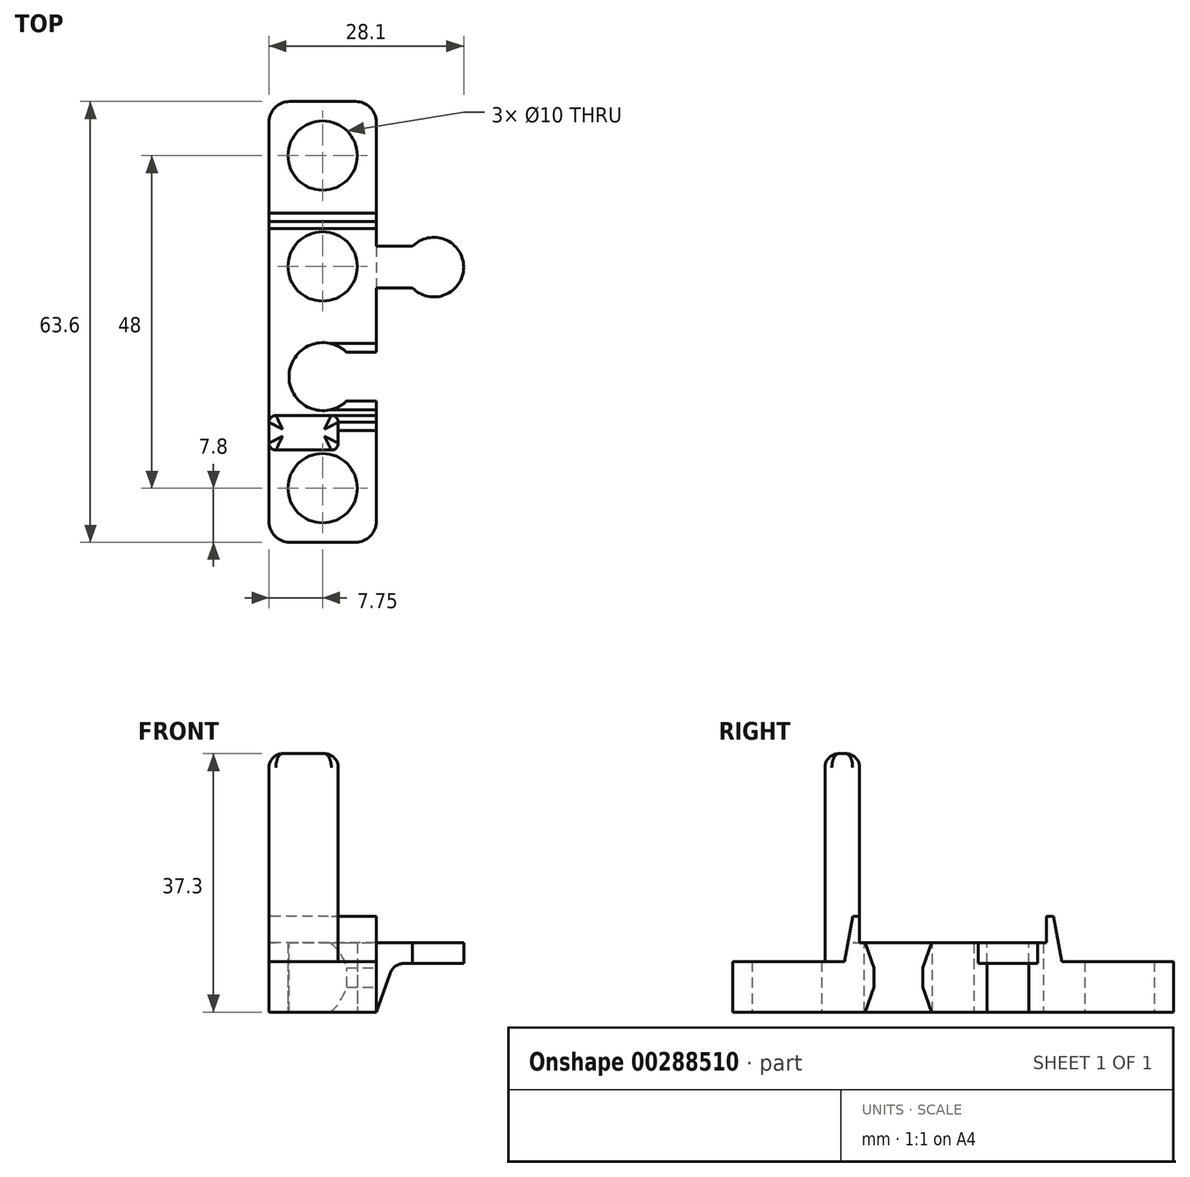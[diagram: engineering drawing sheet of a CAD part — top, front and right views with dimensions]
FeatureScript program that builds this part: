
annotation { "Feature Type Name" : "Feature", "Feature Type Description" : "" }
export const myFeature = defineFeature(function(context is Context, id is Id, definition is map)
    precondition{}
    {
        {
            var Q0;
            Q0=qCreatedBy(makeId("Right.planeOp"),FACE);
            var sketch = newSketch(context, id + "F0", { "sketchPlane" : qUnion([Q0])});
            skLineSegment(sketch, "E0", {"start": v(-31.8, 0) * mm, "end": v(31.8, 0) * mm});
            skLineSegment(sketch, "E1", {"start": v(31.8, 0) * mm, "end": v(31.8, 6.5) * mm});
            skLineSegment(sketch, "E2", {"start": v(31.8, 6.5) * mm, "end": v(27, 6.5) * mm});
            skLineSegment(sketch, "E3", {"start": v(27, 6.5) * mm, "end": v(27, 7.3) * mm});
            skLineSegment(sketch, "E4", {"start": v(27, 7.3) * mm, "end": v(15.7, 7.3) * mm});
            skLineSegment(sketch, "E5", {"start": v(15.7, 7.3) * mm, "end": v(14.5, 13.8) * mm});
            skLineSegment(sketch, "E6", {"start": v(14.5, 13.8) * mm, "end": v(13.5, 13.8) * mm});
            skLineSegment(sketch, "E7", {"start": v(13.5, 13.8) * mm, "end": v(13.5, 10) * mm});
            skLineSegment(sketch, "E8", {"start": v(13.5, 10) * mm, "end": v(-13.5, 10) * mm});
            skLineSegment(sketch, "E9", {"start": v(-13.5, 10) * mm, "end": v(-13.5, 13.8) * mm});
            skLineSegment(sketch, "E10", {"start": v(-13.5, 13.8) * mm, "end": v(-14.5, 13.8) * mm});
            skLineSegment(sketch, "E11", {"start": v(-14.5, 13.8) * mm, "end": v(-15.7, 7.3) * mm});
            skLineSegment(sketch, "E12", {"start": v(-15.7, 7.3) * mm, "end": v(-27, 7.3) * mm});
            skLineSegment(sketch, "E13", {"start": v(-27, 7.3) * mm, "end": v(-27, 6.5) * mm});
            skLineSegment(sketch, "E14", {"start": v(-27, 6.5) * mm, "end": v(-31.8, 6.5) * mm});
            skLineSegment(sketch, "E15", {"start": v(-31.8, 6.5) * mm, "end": v(-31.8, 0) * mm});
            skLineSegment(sketch, "E16", {"start": v(0, 0) * mm, "end": v(0, 10) * mm, "construction": true});
            skLineSegment(sketch, "E17", {"start": v(31.8, 6.5) * mm, "end": v(31.8, 7.3) * mm});
            skLineSegment(sketch, "E18", {"start": v(31.8, 7.3) * mm, "end": v(27, 7.3) * mm});
            skLineSegment(sketch, "E19", {"start": v(-27, 7.3) * mm, "end": v(-31.8, 7.3) * mm});
            skLineSegment(sketch, "E20", {"start": v(-31.8, 7.3) * mm, "end": v(-31.8, 6.5) * mm});
            skSolve(sketch);
        }
        {
            var Q0;
            Q0=makeQuery(id+"F0.imprint","IMPRINT",FACE,{"disambiguationData":[TD([[makeQuery(id+"F0.imprint","IMPRINT",EDGE,{"derivedFrom":sQuery(id+"F0.wireOp",EDGE,"E0")}),1.0]])]});
            var Q1;
            Q1=makeQuery(id+"F0.imprint","IMPRINT",FACE,{"disambiguationData":[TD([[makeQuery(id+"F0.imprint","IMPRINT",EDGE,{"derivedFrom":sQuery(id+"F0.wireOp",EDGE,"E2")}),-1.0]])]});
            var Q2;
            Q2=makeQuery(id+"F0.imprint","IMPRINT",FACE,{"disambiguationData":[TD([[makeQuery(id+"F0.imprint","IMPRINT",EDGE,{"derivedFrom":sQuery(id+"F0.wireOp",EDGE,"E13")}),-1.0]])]});
            extrude(context, id + "F1", {"entities" : qUnion([Q0, Q1, Q2]), "depth" : 15.5 * mm});
        }
        {
            var Q0;
            {var subQ2=sQuery(id+"F0.wireOp",EDGE,"E8");Q0=makeQuery(id+"Fd2kQtNKp41u5WM_1.boolean.opBoolean","SPLIT",FACE,{"disambiguationData":[TD([makeQuery(id+"Fd2kQtNKp41u5WM_1.opExtrude","SWEPT_FACE",FACE,{"disambiguationData":[OSD([sQuery(id+"FLYgMF3d6I8RyJO_1.wireOp",EDGE,"WrdMHGEj-RwoE-VCyH-XmJf-NVLhvrugVPG2.left")])]})])],"derivedFrom":makeQuery(id+"F1.opExtrude","SWEPT_FACE",FACE,{"disambiguationData":[OSD([subQ2])]})});}
            var sketch = newSketch(context, id + "F2", { "sketchPlane" : qUnion([Q0])});
            skLineSegment(sketch, "E21.0", {"start": v(15.5, 13.5) * mm, "end": v(15.5, -13.5) * mm});
            skLineSegment(sketch, "E22", {"start": v(15.5, 10.9) * mm, "end": v(20.72, 10.9) * mm});
            skArc(sketch, "E23", {"start": v(20.72, 10.9) * mm, "mid": v(28.1, 7.9) * mm, "end": v(20.72, 4.9) * mm});
            skLineSegment(sketch, "E24", {"start": v(20.72, 4.9) * mm, "end": v(15.5, 4.9) * mm});
            skSolve(sketch);
        }
        {
            var Q0;
            {var subQ0=sQuery(id+"F2.wireOp",EDGE,"E22");Q0=makeQuery(id+"F2.imprint","IMPRINT",FACE,{"disambiguationData":[TD([[makeQuery(id+"F2.imprint","IMPRINT",EDGE,{"derivedFrom":subQ0}),-1.0]])]});}
            var Q1;
            Q1=makeQuery(id+"F1.opExtrude","SWEPT_FACE",FACE,{"disambiguationData":[OSD([sQuery(id+"F0.wireOp",EDGE,"E0")])]});
            extrude(context, id + "F3", {"entities" : qUnion([Q0]), "operationType" : NewBodyOperationType.ADD, "endBound" : BoundingType.UP_TO_SURFACE, "oppositeDirection" : true, "endBoundEntityFace" : qUnion([Q1]), "depth" : 25 * mm});
        }
        {
            var Q0;
            Q0=makeQuery(id+"F3.boolean.opBoolean","MERGE",FACE,{"derivedFrom":[makeQuery(id+"F1.opExtrude","SWEPT_FACE",FACE,{"disambiguationData":[OSD([sQuery(id+"F0.wireOp",EDGE,"E8")])]}),makeQuery(id+"F3.opExtrude","CAP_FACE",FACE,{"disambiguationData":[OSD([sQuery(id+"F2.wireOp",EDGE,"E21.0"),sQuery(id+"F2.wireOp",EDGE,"E22"),sQuery(id+"F2.wireOp",EDGE,"E23"),sQuery(id+"F2.wireOp",EDGE,"E24")])],"isStart":true})]});
            var sketch = newSketch(context, id + "F4", { "sketchPlane" : qUnion([Q0])});
            skLineSegment(sketch, "E25.0", {"start": v(15.5, 4.9) * mm, "end": v(15.5, -13.5) * mm});
            skArc(sketch, "E26", {"start": v(11.23, -4.4) * mm, "mid": v(2.9, -7.9) * mm, "end": v(11.23, -11.4) * mm});
            skLineSegment(sketch, "E27", {"start": v(11.23, -4.4) * mm, "end": v(15.5, -4.4) * mm});
            skLineSegment(sketch, "E28", {"start": v(11.23, -11.4) * mm, "end": v(15.5, -11.4) * mm});
            skLineSegment(sketch, "E29", {"start": v(7.8, -7.9) * mm, "end": v(15.5, -7.9) * mm, "construction": true});
            skSolve(sketch);
        }
        {
            var Q0;
            Q0=makeQuery(id+"F4.imprint","IMPRINT",FACE,{"disambiguationData":[TD([[makeQuery(id+"F4.imprint","IMPRINT",EDGE,{"derivedFrom":sQuery(id+"F4.wireOp",EDGE,"E26")}),1.0]])]});
            extrude(context, id + "F5", {"entities" : qUnion([Q0]), "operationType" : NewBodyOperationType.REMOVE, "endBound" : BoundingType.THROUGH_ALL, "oppositeDirection" : true, "depth" : 25 * mm});
        }
        {
            var Q0;
            Q0=qCreatedBy(makeId("Front.planeOp"),FACE);
            var sketch = newSketch(context, id + "F6", { "sketchPlane" : qUnion([Q0])});
            skLineSegment(sketch, "E30.0", {"start": v(20.72, 10) * mm, "end": v(28.1, 10) * mm});
            skLineSegment(sketch, "E31.0", {"start": v(15.5, 0) * mm, "end": v(15.5, 10) * mm});
            skLineSegment(sketch, "E32", {"start": v(28.1, 7) * mm, "end": v(28.1, 10) * mm});
            skLineSegment(sketch, "E33", {"start": v(28.1, 0) * mm, "end": v(28.1, 7) * mm});
            skLineSegment(sketch, "E34", {"start": v(15.5, 0) * mm, "end": v(28.1, 0) * mm});
            skLineSegment(sketch, "E35", {"start": v(28.1, 7) * mm, "end": v(18, 7) * mm});
            skLineSegment(sketch, "E36", {"start": v(18, 7) * mm, "end": v(15.5, 0) * mm});
            skSolve(sketch);
        }
        {
            var Q0;
            Q0=makeQuery(id+"F6.imprint","IMPRINT",FACE,{"disambiguationData":[TD([[makeQuery(id+"F6.imprint","IMPRINT",EDGE,{"derivedFrom":sQuery(id+"F6.wireOp",EDGE,"ok0Bq9OS-mmUX-e6rK-MkHC-rcdQiOLZ93gB")}),-1.0]])]});
            var Q1;
            Q1=makeQuery(id+"F6.imprint","IMPRINT",FACE,{"disambiguationData":[TD([[makeQuery(id+"F6.imprint","IMPRINT",EDGE,{"derivedFrom":sQuery(id+"F6.wireOp",EDGE,"E33")}),1.0]])]});
            extrude(context, id + "F7", {"entities" : qUnion([Q0, Q1]), "operationType" : NewBodyOperationType.REMOVE, "endBound" : BoundingType.THROUGH_ALL, "oppositeDirection" : true, "depth" : 25 * mm});
        }
        {
            var Q0;
            {var subQ0=sQuery(id+"F2.wireOp",EDGE,"E24");var subQ5=sQuery(id+"F0.wireOp",EDGE,"E8");var subQ8=sQuery(id+"F0.wireOp",EDGE,"E0");var subQ10=makeQuery(id+"F3.opExtrude","SWEPT_FACE",FACE,{"disambiguationData":[OSD([subQ0])]});var subQ11=sQuery(id+"F0.wireOp",EDGE,"E9");var subQ12=sQuery(id+"F0.wireOp",EDGE,"E10");var subQ13=sQuery(id+"F0.wireOp",EDGE,"E11");var subQ14=sQuery(id+"F0.wireOp",EDGE,"E19");var subQ15=sQuery(id+"F0.wireOp",EDGE,"E12");var subQ16=sQuery(id+"F0.wireOp",EDGE,"E20");var subQ17=sQuery(id+"F0.wireOp",EDGE,"E15");Q0=makeQuery(id+"F5.boolean.opBoolean","SPLIT",FACE,{"disambiguationData":[TD([subQ10])],"derivedFrom":makeQuery(id+"F3.boolean.opBoolean","SPLIT",FACE,{"disambiguationData":[TD([makeQuery(id+"F1.opExtrude","SWEPT_FACE",FACE,{"disambiguationData":[OSD([subQ11])]})])],"derivedFrom":makeQuery(id+"F1.opExtrude","CAP_FACE",FACE,{"disambiguationData":[OSD([subQ8,sQuery(id+"F0.wireOp",EDGE,"E1"),sQuery(id+"F0.wireOp",EDGE,"E4"),sQuery(id+"F0.wireOp",EDGE,"E5"),sQuery(id+"F0.wireOp",EDGE,"E6"),sQuery(id+"F0.wireOp",EDGE,"E7"),subQ5,subQ11,subQ12,subQ13,subQ15,subQ17,sQuery(id+"F0.wireOp",EDGE,"E17"),sQuery(id+"F0.wireOp",EDGE,"E18"),subQ14,subQ16])],"isStart":false})})});}
            var sketch = newSketch(context, id + "F8", { "sketchPlane" : qUnion([Q0])});
            skLineSegment(sketch, "E37.0", {"start": v(-4.4, 0) * mm, "end": v(-4.4, 10) * mm});
            skLineSegment(sketch, "E38.0", {"start": v(-11.4, 0) * mm, "end": v(-11.4, 10) * mm});
            skLineSegment(sketch, "E39.0", {"start": v(-11.4, 10) * mm, "end": v(-13.5, 10) * mm});
            skLineSegment(sketch, "E40.0", {"start": v(4.9, 10) * mm, "end": v(-4.4, 10) * mm});
            skLineSegment(sketch, "E41.0", {"start": v(-4.4, 0) * mm, "end": v(4.9, 0) * mm});
            skLineSegment(sketch, "E42.0", {"start": v(-31.8, 0) * mm, "end": v(-11.4, 0) * mm});
            skLineSegment(sketch, "E43", {"start": v(-12.7, 10) * mm, "end": v(-11.4, 6.4) * mm});
            skLineSegment(sketch, "E44", {"start": v(-11.4, 3.6) * mm, "end": v(-12.7, 0) * mm});
            skLineSegment(sketch, "E45", {"start": v(-4.4, 6.4) * mm, "end": v(-3.1, 10) * mm});
            skLineSegment(sketch, "E46", {"start": v(-4.4, 3.6) * mm, "end": v(-3.1, 0) * mm});
            skSolve(sketch);
        }
        {
            var Q0;
            {var subQ3=sQuery(id+"F8.wireOp",EDGE,"E45");Q0=makeQuery(id+"F8.imprint","IMPRINT",FACE,{"disambiguationData":[TD([[makeQuery(id+"F8.imprint","IMPRINT",EDGE,{"derivedFrom":subQ3}),1.0]])]});}
            var Q1;
            {var subQ3=sQuery(id+"F8.wireOp",EDGE,"E46");Q1=makeQuery(id+"F8.imprint","IMPRINT",FACE,{"disambiguationData":[TD([[makeQuery(id+"F8.imprint","IMPRINT",EDGE,{"derivedFrom":subQ3}),-1.0]])]});}
            var Q2;
            {var subQ3=sQuery(id+"F8.wireOp",EDGE,"E44");Q2=makeQuery(id+"F8.imprint","IMPRINT",FACE,{"disambiguationData":[TD([[makeQuery(id+"F8.imprint","IMPRINT",EDGE,{"derivedFrom":subQ3}),1.0]])]});}
            var Q3;
            {var subQ3=sQuery(id+"F8.wireOp",EDGE,"E43");Q3=makeQuery(id+"F8.imprint","IMPRINT",FACE,{"disambiguationData":[TD([[makeQuery(id+"F8.imprint","IMPRINT",EDGE,{"derivedFrom":subQ3}),1.0]])]});}
            extrude(context, id + "F9", {"entities" : qUnion([Q0, Q1, Q2, Q3]), "operationType" : NewBodyOperationType.REMOVE, "oppositeDirection" : true, "depth" : 8 * mm});
        }
        {
            var Q0;
            Q0=makeQuery(id+"F3.boolean.opBoolean","MERGE",FACE,{"derivedFrom":[makeQuery(id+"F1.opExtrude","SWEPT_FACE",FACE,{"disambiguationData":[OSD([sQuery(id+"F0.wireOp",EDGE,"E0")])]}),makeQuery(id+"F3.opExtrude","CAP_FACE",FACE,{"disambiguationData":[OSD([sQuery(id+"F2.wireOp",EDGE,"E21.0"),sQuery(id+"F2.wireOp",EDGE,"E22"),sQuery(id+"F2.wireOp",EDGE,"E23"),sQuery(id+"F2.wireOp",EDGE,"E24")])],"isStart":false})]});
            var sketch = newSketch(context, id + "F10", { "sketchPlane" : qUnion([Q0])});
            skCircle(sketch, "E47", {"center": v(7.75, -24) * mm, "radius": 5 * mm});
            skLineSegment(sketch, "E48", {"start": v(0, 0) * mm, "end": v(15.5, 0) * mm, "construction": true});
            skPoint(sketch, "E48.endSnap0", {"position": v(0, 0) * mm});
            skLineSegment(sketch, "E49.0", {"start": v(15.5, 3.1) * mm, "end": v(15.5, -4.9) * mm});
            skCircle(sketch, "E50.0.1.0", {"center": v(7.75, -8) * mm, "radius": 5 * mm});
            skCircle(sketch, "E50.0.2.0", {"center": v(7.75, 8) * mm, "radius": 5 * mm});
            skCircle(sketch, "E50.0.3.0", {"center": v(7.75, 24) * mm, "radius": 5 * mm});
            skLineSegment(sketch, "E50.direction1", {"start": v(7.75, -24) * mm, "end": v(32.75, -24) * mm, "construction": true});
            skLineSegment(sketch, "E50.direction2", {"start": v(7.75, -24) * mm, "end": v(7.75, -8) * mm, "construction": true});
            skSolve(sketch);
        }
        {
            var Q0;
            Q0=makeQuery(id+"F10.imprint","IMPRINT",FACE,{"disambiguationData":[TD([[makeQuery(id+"F10.imprint","IMPRINT",EDGE,{"derivedFrom":sQuery(id+"F10.wireOp",EDGE,"E50.0.3.0")}),1.0]])]});
            var Q1;
            Q1=makeQuery(id+"F10.imprint","IMPRINT",FACE,{"disambiguationData":[TD([[makeQuery(id+"F10.imprint","IMPRINT",EDGE,{"derivedFrom":sQuery(id+"F10.wireOp",EDGE,"E50.0.1.0")}),1.0]])]});
            var Q2;
            Q2=makeQuery(id+"F10.imprint","IMPRINT",FACE,{"disambiguationData":[TD([[makeQuery(id+"F10.imprint","IMPRINT",EDGE,{"derivedFrom":sQuery(id+"F10.wireOp",EDGE,"E47")}),1.0]])]});
            extrude(context, id + "F11", {"entities" : qUnion([Q0, Q1, Q2]), "operationType" : NewBodyOperationType.REMOVE, "endBound" : BoundingType.THROUGH_ALL, "oppositeDirection" : true, "depth" : 25 * mm});
        }
        {
            var Q0;
            Q0=makeQuery(id+"F1.opExtrude","CAP_EDGE",EDGE,{"disambiguationData":[OSD([sQuery(id+"F0.wireOp",EDGE,"E15"),sQuery(id+"F0.wireOp",EDGE,"E20")])],"isStart":true});
            var Q1;
            Q1=makeQuery(id+"F1.opExtrude","CAP_EDGE",EDGE,{"disambiguationData":[OSD([sQuery(id+"F0.wireOp",EDGE,"E15"),sQuery(id+"F0.wireOp",EDGE,"E20")])],"isStart":false});
            var Q2;
            Q2=makeQuery(id+"F1.opExtrude","CAP_EDGE",EDGE,{"disambiguationData":[OSD([sQuery(id+"F0.wireOp",EDGE,"E1"),sQuery(id+"F0.wireOp",EDGE,"E17")])],"isStart":false});
            var Q3;
            Q3=makeQuery(id+"F1.opExtrude","CAP_EDGE",EDGE,{"disambiguationData":[OSD([sQuery(id+"F0.wireOp",EDGE,"E1"),sQuery(id+"F0.wireOp",EDGE,"E17")])],"isStart":true});
            fillet(context, id + "F12", {"entities" : qUnion([Q0, Q1, Q2, Q3]), "radius" : 3 * mm, "tangentPropagation" : true, "allowEdgeOverflow" : false});
        }
        {
            var Q0;
            Q0=makeQuery(id+"F1.opExtrude","SWEPT_FACE",FACE,{"disambiguationData":[OSD([sQuery(id+"F0.wireOp",EDGE,"E9")])]});
            var sketch = newSketch(context, id + "F13", { "sketchPlane" : qUnion([Q0])});
            skLineSegment(sketch, "E51.0", {"start": v(0, 10) * mm, "end": v(0, 13.8) * mm});
            skLineSegment(sketch, "E52", {"start": v(0, 13.8) * mm, "end": v(0, 37.3) * mm});
            skLineSegment(sketch, "E53", {"start": v(0, 37.3) * mm, "end": v(-10, 37.3) * mm});
            skLineSegment(sketch, "E54", {"start": v(0, 10) * mm, "end": v(0, 7.3) * mm});
            skLineSegment(sketch, "E55", {"start": v(0, 7.3) * mm, "end": v(-10, 7.3) * mm});
            skLineSegment(sketch, "E56", {"start": v(-10, 7.3) * mm, "end": v(-10, 37.3) * mm});
            skSolve(sketch);
        }
        {
            var Q0;
            Q0 = qSketchRegion(id + "F13", true);
            extrude(context, id + "F14", {"entities" : qUnion([Q0]), "operationType" : NewBodyOperationType.ADD, "oppositeDirection" : true, "depth" : 5 * mm});
        }
        {
            var Q0;
            Q0=makeQuery(id+"F14.opExtrude","CAP_EDGE",EDGE,{"disambiguationData":[OSD([sQuery(id+"F13.wireOp",EDGE,"E56")])],"isStart":true});
            var Q1;
            Q1=makeQuery(id+"F14.opExtrude","CAP_EDGE",EDGE,{"disambiguationData":[OSD([sQuery(id+"F13.wireOp",EDGE,"E56")])],"isStart":false});
            var Q2;
            Q2=makeQuery(id+"F14.opExtrude","CAP_EDGE",EDGE,{"disambiguationData":[OSD([sQuery(id+"F13.wireOp",EDGE,"E51.0"),sQuery(id+"F13.wireOp",EDGE,"E52"),sQuery(id+"F13.wireOp",EDGE,"E54")])],"isStart":false});
            var Q3;
            Q3=makeQuery(id+"F14.boolean.opBoolean","MERGE",EDGE,{"derivedFrom":[makeQuery(id+"F1.opExtrude","CAP_EDGE",EDGE,{"disambiguationData":[OSD([sQuery(id+"F0.wireOp",EDGE,"E9")])],"isStart":true}),makeQuery(id+"F14.opExtrude","CAP_EDGE",EDGE,{"disambiguationData":[OSD([sQuery(id+"F13.wireOp",EDGE,"E51.0"),sQuery(id+"F13.wireOp",EDGE,"E52"),sQuery(id+"F13.wireOp",EDGE,"E54")])],"isStart":true})]});
            fillet(context, id + "F15", {"entities" : qUnion([Q0, Q1, Q2, Q3]), "radius" : 1 * mm, "tangentPropagation" : true, "allowEdgeOverflow" : false});
        }
        {
            var Q0;
            Q0=makeQuery(id+"F14.opExtrude","CAP_EDGE",EDGE,{"disambiguationData":[OSD([sQuery(id+"F13.wireOp",EDGE,"E53")])],"isStart":false});
            fillet(context, id + "F16", {"entities" : qUnion([Q0]), "radius" : 2 * mm, "tangentPropagation" : true, "allowEdgeOverflow" : false});
        }
        {
            var Q0;
            Q0=makeQuery(id+"F7.boolean.opBoolean","COPY",EDGE,{"derivedFrom":makeQuery(id+"F7.opExtrude","SWEPT_EDGE",EDGE,{"disambiguationData":[OSD([sQuery(id+"F6.wireOp",EDGE,"E35"),sQuery(id+"F6.wireOp",EDGE,"E36")])]})});
            fillet(context, id + "F17", {"entities" : qUnion([Q0]), "radius" : 2 * mm, "tangentPropagation" : true, "allowEdgeOverflow" : false});
        }
    });
